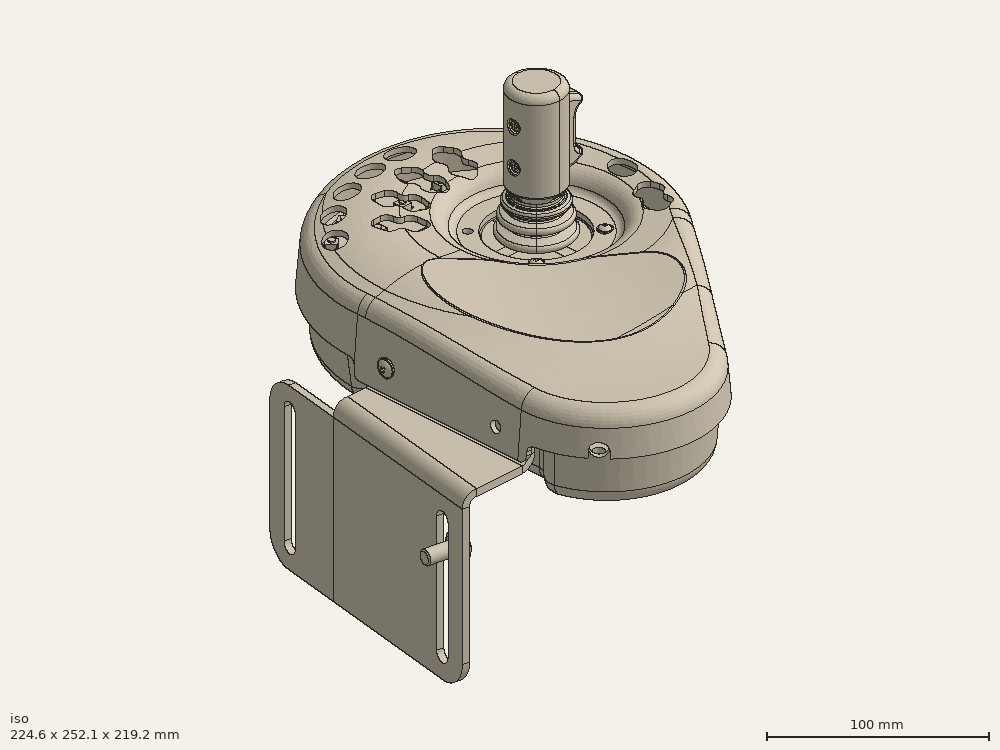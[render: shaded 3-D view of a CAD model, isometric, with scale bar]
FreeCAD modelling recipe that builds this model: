
FCSTD DOCUMENT  (FreeCAD 0.17R6700 (Git))
Label: assembly
License: All rights reserved
LicenseURL: http://en.wikipedia.org/wiki/All_rights_reserved
objects: Part::FeaturePython×14, Part::Feature×4
note: 18 computed .brp shape members not serialized (recipe doc carries the construction recipe); baked Part::Feature solids carry a one-line shape summary decoded from their .brp

FEATURE [Part::Feature] Part__Feature  label="joy"
  Placement = pos=(0,0,-16.1) rot=(0.57735,-0.57735,-0.57735;2.0944rad)
  shape: bbox 17.66 x 57.66 x 25.13 mm, 562 faces (baked)
FEATURE [Part::Feature] Part__Feature001  label="joy001"
  Placement = pos=(0,0,-16.1) rot=(0.57735,-0.57735,-0.57735;2.0944rad)
  shape: bbox 74.63 x 74.63 x 129.8 mm, 2403 faces (baked)
FEATURE [Part::Feature] Part__Feature002  label="joy002"
  Placement = pos=(0,0,-16.1) rot=(0.57735,-0.57735,-0.57735;2.0944rad)
  shape: bbox 11.11 x 11.11 x 64.77 mm, 36 faces (baked)
FEATURE [Part::Feature] Part__Feature003  label="joy003"
  Placement = pos=(0,0,-16.1) rot=(0.57735,-0.57735,-0.57735;2.0944rad)
  shape: bbox 23.77 x 72.14 x 51.34 mm, 195 faces (baked)
FEATURE [Part::FeaturePython] collar_bottom_01  # a2plus imported part (geometry in sourceFile) (typed FeaturePython)
  fixedPosition = false
  sourceFile = <userpath>/uw/keypad/hw/collar_bottom.fcstd
  timeLastImport = 1.53148e+09
  updateColors = true
FEATURE [Part::FeaturePython] left2_01  label="pcb"  # a2plus imported part (geometry in sourceFile) (typed FeaturePython)
  Placement = pos=(-16,18.4313,-4) rot=(0,0,1;0rad)
  fixedPosition = false
  sourceFile = <userpath>/uw/keypad/hw/left2.FCStd
  timeLastImport = 1.51211e+09
  updateColors = true
FEATURE [Part::FeaturePython] Screw  label="M4x20-Screw"  # Fasteners workbench fastener (typed FeaturePython)
  Placement = pos=(-110.5,-85,-16.9) rot=(0,-1,0;1.5708rad)
  diameter = 3
  invert = false
  length = 7
  matchOuter = false
  offset = 0
  thread = false
  type = 0
FEATURE [Part::FeaturePython] Clone  label="Clone of M4x8-Screw"  # Draft clone (typed FeaturePython)
  Objects = -> [Screw]
  Placement = pos=(-110.5,-15,-16.9) rot=(0,-1,0;1.5708rad)
  Scale = (1,1,1)
FEATURE [Part::FeaturePython] Screw001  label="M3x14-Screw"  # Fasteners workbench fastener (typed FeaturePython)
  Placement = pos=(-21.93,21.93,4) rot=(0,0,1;0rad)
  diameter = 1
  invert = false
  length = 6
  matchOuter = false
  offset = 0
  thread = false
  type = 0
FEATURE [Part::FeaturePython] Clone001  label="Clone of M3x14-Screw"  # Draft clone (typed FeaturePython)
  Objects = -> [Screw001]
  Placement = pos=(21.93,-21.93,4) rot=(0,0,1;0rad)
  Scale = (1,1,1)
FEATURE [Part::FeaturePython] Clone002  label="Clone of M3x14-Screw001"  # Draft clone (typed FeaturePython)
  Objects = -> [Screw001]
  Placement = pos=(-21.93,-21.93,4) rot=(0,0,1;0rad)
  Scale = (1,1,1)
FEATURE [Part::FeaturePython] Clone003  label="Clone of M3x14-Screw002"  # Draft clone (typed FeaturePython)
  Objects = -> [Screw001]
  Placement = pos=(21.93,21.93,4) rot=(0,0,1;0rad)
  Scale = (1,1,1)
FEATURE [Part::FeaturePython] Screw002  label="M8x16-Screw"  # Fasteners workbench fastener (typed FeaturePython)
  Placement = pos=(-119.891,34.3056,-71.5) rot=(0.173648,0.984808,0;1.5708rad)
  diameter = 9
  invert = false
  length = 0
  matchOuter = false
  offset = 0
  thread = false
  type = 14
FEATURE [Part::FeaturePython] Clone004  label="Clone of M8x16-Screw"  # Draft clone (typed FeaturePython)
  Objects = -> [Screw002]
  Placement = pos=(-137.256,-84.1752,-71.5) rot=(0.173648,0.984808,0;1.5708rad)
  Scale = (1,1,1)
FEATURE [Part::FeaturePython] collar_top_01  # a2plus imported part (geometry in sourceFile) (typed FeaturePython)
  fixedPosition = true
  sourceFile = <userpath>/uw/keypad/hw/collar_top.fcstd
  timeLastImport = 1.52985e+09
  updateColors = true
FEATURE [Part::FeaturePython] mounting_metal_01  # a2plus imported part (geometry in sourceFile) (typed FeaturePython)
  fixedPosition = false
  sourceFile = <userpath>/uw/keypad/hw/mounting_metal.fcstd
  timeLastImport = 1.52985e+09
  updateColors = true
FEATURE [Part::FeaturePython] UV07_MJO002_01  # a2plus imported part (geometry in sourceFile) (typed FeaturePython)
  Placement = pos=(0,0,63) rot=(0,0,1;0rad)
  fixedPosition = false
  sourceFile = <userpath>/uv/projects/uv07_mjo/hw/UV07_MJO002.fcstd
  timeLastImport = 1.52917e+09
  updateColors = true
FEATURE [Part::FeaturePython] UV07_MJO014_01  # a2plus imported part (geometry in sourceFile) (typed FeaturePython)
  Placement = pos=(0,0,63) rot=(0,0,1;0rad)
  fixedPosition = false
  sourceFile = <userpath>/uv/projects/uv07_mjo/hw/UV07_MJO014.fcstd
  timeLastImport = 1.52917e+09
  updateColors = true
